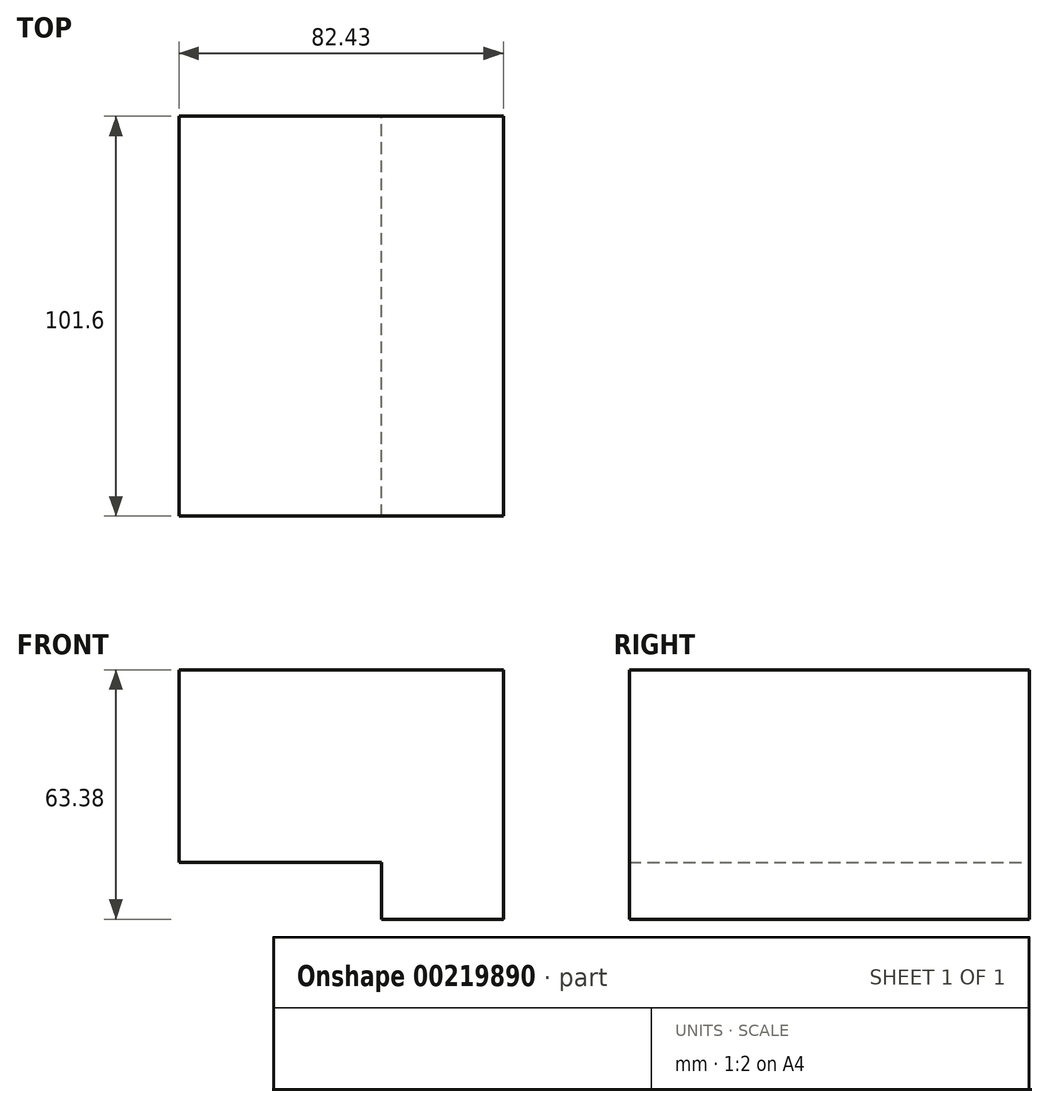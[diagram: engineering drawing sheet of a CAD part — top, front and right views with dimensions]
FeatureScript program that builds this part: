
annotation { "Feature Type Name" : "Feature", "Feature Type Description" : "" }
export const myFeature = defineFeature(function(context is Context, id is Id, definition is map)
    precondition{}
    {
        {
            var Q0;
            Q0=qCreatedBy(makeId("Front.planeOp"),FACE);
            var sketch = newSketch(context, id + "F0", { "sketchPlane" : qUnion([Q0])});
            skLineSegment(sketch, "E0", {"start": v(0, 0) * mm, "end": v(0, 63.38) * mm});
            skLineSegment(sketch, "E1", {"start": v(0, 63.38) * mm, "end": v(-82.43, 63.38) * mm});
            skLineSegment(sketch, "E2", {"start": v(-82.43, 63.38) * mm, "end": v(-82.43, 14.43) * mm});
            skLineSegment(sketch, "E3", {"start": v(-82.43, 14.43) * mm, "end": v(-30.94, 14.43) * mm});
            skLineSegment(sketch, "E4", {"start": v(-30.94, 14.43) * mm, "end": v(-30.94, 0) * mm});
            skLineSegment(sketch, "E5", {"start": v(-30.94, 0) * mm, "end": v(0, 0) * mm});
            skSolve(sketch);
        }
        {
            var Q0;
            Q0 = qSketchRegion(id + "F0", true);
            extrude(context, id + "F1", {"entities" : qUnion([Q0]), "endBound" : BoundingType.SYMMETRIC, "depth" : 101.6 * mm});
        }
    });
